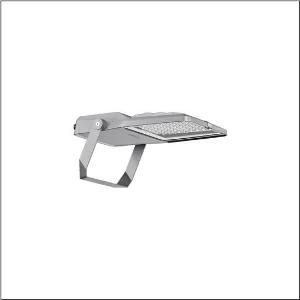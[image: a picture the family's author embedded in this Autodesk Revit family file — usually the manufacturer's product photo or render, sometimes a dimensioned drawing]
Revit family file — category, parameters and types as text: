
# Revit family: floodlight_fl_21_iq_mini___rs12_5xa7772d3b1a_ff90
name_source: partatom
category: Lighting Fixtures
units: mm (PartAtom-declared; Revit-internal decimal feet)

## family parameters
Cut with Voids When Loaded = No
Host = Face
Light Source = No
Part Type = Normal
Room Calculation Point = No
Round Connector Dimension = Use Diameter
Shared = No

## types (1)
- --- (1 x LED, 15500 lm, 143 W, 3000K)
    Apparent Load = 143 VA
    CIE Flux Codes = 79 92 99 100 100
    Color Rendering = 80
    Color Temperature = 3000K
    Default Elevation = 1800 mm
    Description = Floodlight FL 21 iQ mini, floodlight, primary light control with lens, of PMMA, primary optical cover: protective disc, of toughened safety glass, transparent, light distribution: RS12, light emission: direct distribution, installation type: surface-mounted, LED, High Power LED, rated luminous flux: 15.500lm, luminous efficacy: 108lm/W, light colour: 830, colour temperature: 3000K, control: Street-Remote, Auto-Match, Temp-Guard, Night-Set, Smart-Wire, Desk-Remote (wireless, voltage-free reading and setting of iQ features in the workshop via application-optimized NFC function/RFID function), optimised constant luminous flux control (CLO 2.0), with terminal, 6-pole, mains connection: 220..240V, AC, 50/60Hz, start of lifetime: 143W, end of service life: 152W, reduction: 61W, luminaire housing, of diecast aluminium, powder-coated, Siteco® metallic grey (DB 702S), corrosivity category C5 mid according to DIN EN ISO 12944, sealing non-destructively replaceable, mounting bracket, of steel, galvanised, powder-coated, Siteco® metallic grey (DB 702S), protection rating (complete): IP66, insulation class (complete): insulation class II (safety insulation), certification: CE, ENEC, VDE, protection symbol: D, impact resistance: IK08, permissible operating ambient temperature: -40..+40°C, permissible operating ambient temperature for outdoor applications: -40..+50°C, standard: DIN EN 12944, LABS conformity tested according to VDMA 24364:2018-05, packaging unit: 1 piece

Light Distribution: RS12
    Height = 70 mm
    Lamp = 1 x LED
    Lamp Light Flux = 15500 lm
    Lamp Power = 143 W
    Lamp count = 1
    Length = 485 mm
    Luminous efficacy = 108 lm/W
    Manufacturer = Siteco
    ModVariant = No
    Model = 5XA7772D3B1A
    Number of Poles = 1
    OnlyDefault = Yes
    Power Factor = 1
    Product Name = Floodlight FL 21 iQ mini | RS12
    Product group = floodlight | pylon annexe
    ProductGroupID = 6200
    Protection Class = Protection class II
    Protection Degree = IP 66
    RLX_Detail_Level = 1
    RLX_Emergency_Light_Flux = 0 lm
    RLX_Emergency_Type = 0
    RLX_Emergency_Type_DB = No
    RlxData = <blob elided: 91129 chars, md5=0f104675>
    Socket = socket
    Standby Power = 0 W
    System Light Flux = 15500 lm
    System Power = 143 W
    Type Comments = factory setting: luminous flux: 100 % | dim-lin: 254 | 730 mA
    Type Image = l_1006845.jpg
    URL = http://relux.com
    VarID = @adj_099653
    Voltage = 0 V
    Weight = 0.00 kg
    Width = 337 mm

## geometry (parser evidence)
native form markers: Blend x4, Sweep x12
no freeform markers — native parametric forms only
